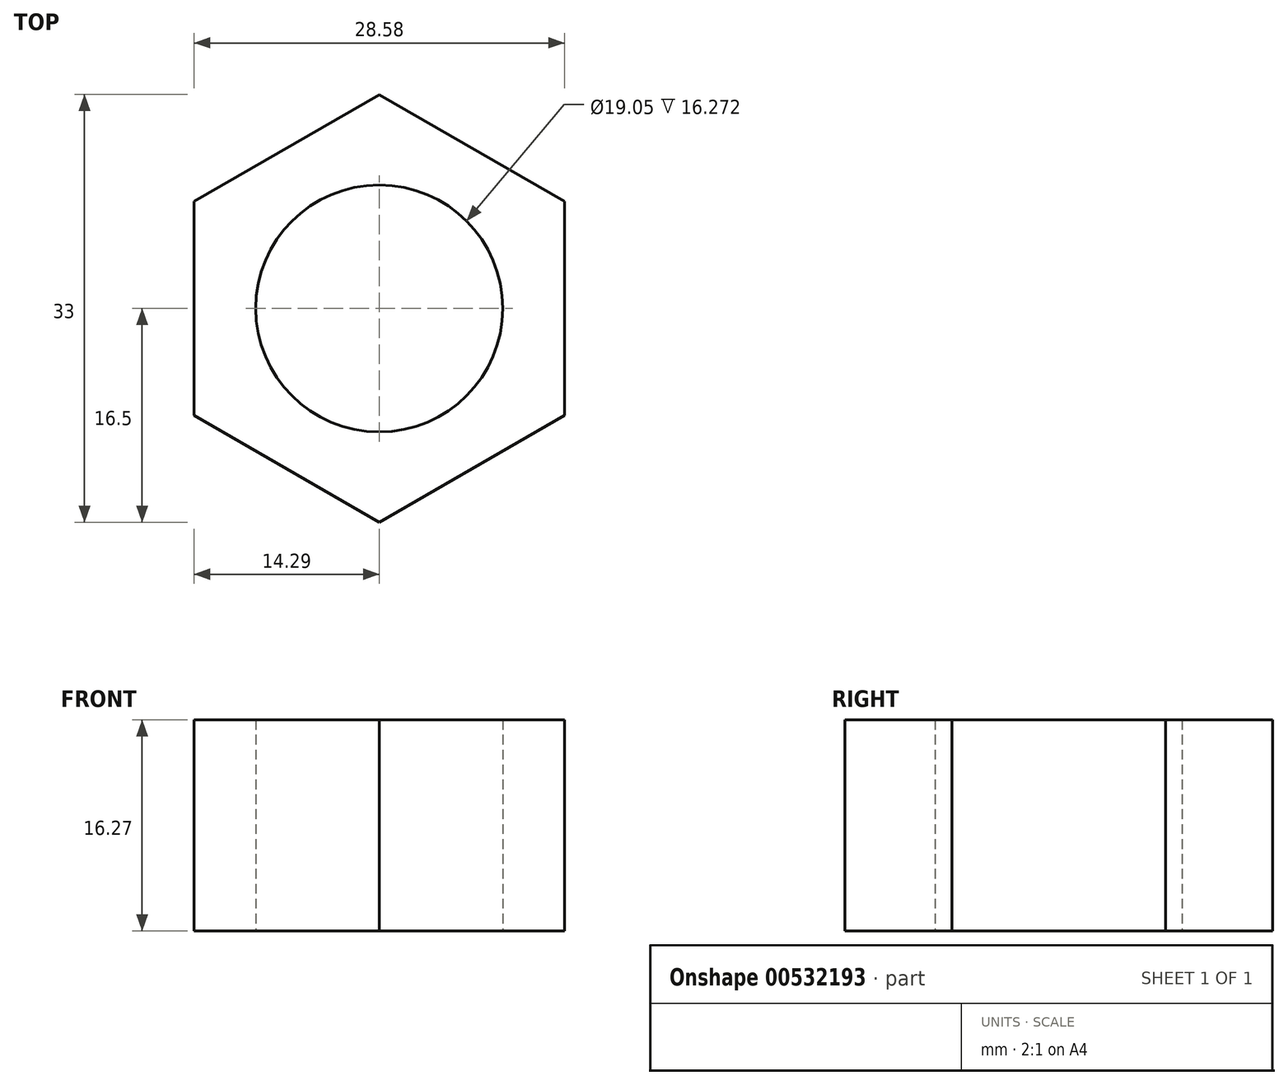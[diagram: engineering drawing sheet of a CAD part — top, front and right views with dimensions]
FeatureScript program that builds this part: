
annotation { "Feature Type Name" : "Feature", "Feature Type Description" : "" }
export const myFeature = defineFeature(function(context is Context, id is Id, definition is map)
    precondition{}
    {
        {
            var Q0;
            Q0=qCreatedBy(makeId("Top.planeOp"),FACE);
            var sketch = newSketch(context, id + "F0", { "sketchPlane" : qUnion([Q0])});
            skCircle(sketch, "E0.cCircle", {"center": v(0, 0) * mm, "radius": 14.29 * mm, "construction": true});
            skLineSegment(sketch, "E0.0", {"start": v(0, 16.5) * mm, "end": v(14.29, 8.25) * mm});
            skLineSegment(sketch, "E0.1", {"start": v(14.29, 8.25) * mm, "end": v(14.29, -8.25) * mm});
            skLineSegment(sketch, "E0.2", {"start": v(14.29, -8.25) * mm, "end": v(0, -16.5) * mm});
            skLineSegment(sketch, "E0.3", {"start": v(0, -16.5) * mm, "end": v(-14.29, -8.25) * mm});
            skLineSegment(sketch, "E0.4", {"start": v(-14.29, -8.25) * mm, "end": v(-14.29, 8.25) * mm});
            skLineSegment(sketch, "E0.5", {"start": v(-14.29, 8.25) * mm, "end": v(0, 16.5) * mm});
            skPoint(sketch, "E0.0.midPoint", {"position": v(7.14, 12.37) * mm});
            skCircle(sketch, "E1", {"center": v(0, 0) * mm, "radius": 9.53 * mm});
            skSolve(sketch);
        }
        {
            var Q0;
            Q0 = qSketchRegion(id + "F0", true);
            extrude(context, id + "F1", {"entities" : qUnion([Q0]), "depth" : 16.27 * mm, "offsetDistance" : 25.4 * mm});
        }
    });
